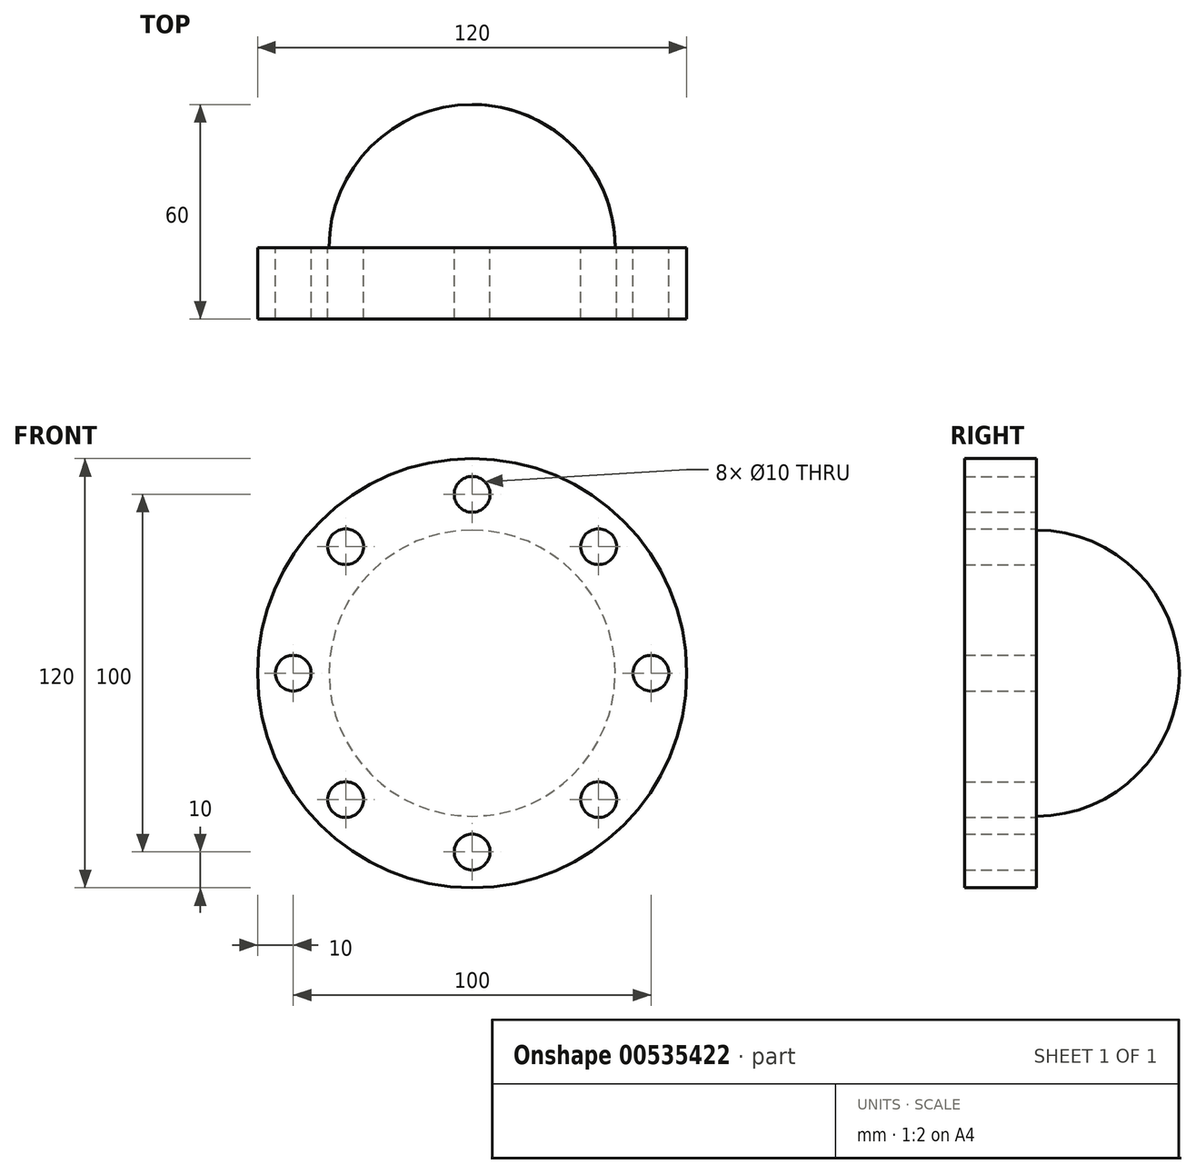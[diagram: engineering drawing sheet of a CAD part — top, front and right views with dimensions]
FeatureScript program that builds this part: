
annotation { "Feature Type Name" : "Feature", "Feature Type Description" : "" }
export const myFeature = defineFeature(function(context is Context, id is Id, definition is map)
    precondition{}
    {
        {
            var Q0;
            Q0=qCreatedBy(makeId("Front.planeOp"),FACE);
            var sketch = newSketch(context, id + "F0", { "sketchPlane" : qUnion([Q0])});
            skCircle(sketch, "E0", {"center": v(0, 0) * mm, "radius": 60 * mm});
            skCircle(sketch, "E1", {"center": v(0, 50) * mm, "radius": 5 * mm});
            skCircle(sketch, "E2.1.0", {"center": v(-35.36, 35.36) * mm, "radius": 5 * mm});
            skCircle(sketch, "E2.2.0", {"center": v(-50, 0) * mm, "radius": 5 * mm});
            skCircle(sketch, "E2.3.0", {"center": v(-35.36, -35.36) * mm, "radius": 5 * mm});
            skCircle(sketch, "E2.4.0", {"center": v(0, -50) * mm, "radius": 5 * mm});
            skCircle(sketch, "E2.5.0", {"center": v(35.36, -35.36) * mm, "radius": 5 * mm});
            skCircle(sketch, "E2.6.0", {"center": v(50, 0) * mm, "radius": 5 * mm});
            skCircle(sketch, "E2.7.0", {"center": v(35.36, 35.36) * mm, "radius": 5 * mm});
            skLineSegment(sketch, "E2.anchor1", {"start": v(0, 0) * mm, "end": v(0, 50) * mm, "construction": true});
            skLineSegment(sketch, "E2.anchor2", {"start": v(0, 0) * mm, "end": v(35.36, 35.36) * mm, "construction": true});
            skSolve(sketch);
        }
        {
            var Q0;
            Q0 = qSketchRegion(id + "F0", true);
            extrude(context, id + "F1", {"entities" : qUnion([Q0]), "depth" : 20 * mm, "offsetDistance" : 25 * mm});
        }
        {
            var Q0;
            Q0=qCreatedBy(makeId("Top.planeOp"),FACE);
            var sketch = newSketch(context, id + "F2", { "sketchPlane" : qUnion([Q0])});
            skPoint(sketch, "E3.orphan", {"position": v(60, 0) * mm});
            skPoint(sketch, "E4.0.end.orphan", {"position": v(-60, 0) * mm});
            skLineSegment(sketch, "E5.0", {"start": v(0, 0) * mm, "end": v(-40, 0) * mm});
            skArc(sketch, "E6", {"start": v(0, 40) * mm, "mid": v(-28.28, 28.28) * mm, "end": v(-40, 0) * mm});
            skLineSegment(sketch, "E7", {"start": v(0, 40) * mm, "end": v(0, 0) * mm});
            skSolve(sketch);
        }
        {
            var Q0;
            Q0 = qSketchRegion(id + "F2", true);
            var Q1;
            Q1=sQuery(id+"F2.wireOp",EDGE,"E7");
            revolve(context, id + "F3", {"operationType" : NewBodyOperationType.ADD, "entities" : qUnion([Q0]), "axis" : qUnion([Q1]), "revolveType" : RevolveType.FULL});
        }
    });
